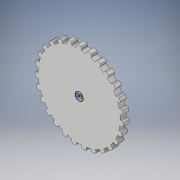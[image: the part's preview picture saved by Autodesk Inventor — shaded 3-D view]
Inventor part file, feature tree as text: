
AUTODESK INVENTOR PART (.ipt)
format: ipt  version: 2017 (Build 210142000, 142)  size: 397,824 bytes
history: native  units: in
note: dims shown in document units (in); Inventor stores cm internally (conversion verified against a paired STEP export)
features: sketch x4, extrude x3, pattern_circular x1
ambient origin geometry x8: Origin, YZ Plane, XZ Plane, XY Plane, X Axis, Y Axis, Z Axis, Center Point
bodies: Solid1 (feature_tree)
feature tree (8):
  extrude  "Extrusion1"  Depth=0.075in
  pattern_circular  "Circular Pattern1"  Count=108 Angle=360.0deg
  extrude  "Extrusion2"  Depth=0.062in
  sketch  "Sketch3"  dims[d6=0.04in d7=42.5197in d9=360.0deg]
  extrude  "Extrusion3"  Depth=0.15in TaperAngle=0.0deg
  sketch  "Sketch1"  dims[d0=2.025in d4=0.075in]
  sketch  "Sketch2"  dims[d5=0.04in]
  sketch  "Sketch4"  dims[d11=0.062in d12=0.062in d13=0.15in d14=0.0in d15=10.6299in d16=360.0deg d18=0.0591in d19=0.15in d20=0.0in d21=0.3862in d22=0.0in]
